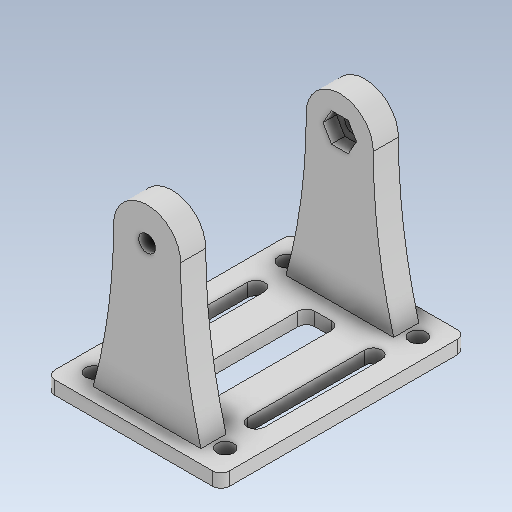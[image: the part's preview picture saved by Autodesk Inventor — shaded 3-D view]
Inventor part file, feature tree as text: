
AUTODESK INVENTOR PART (.ipt)
format: ipt  version: 2020 (Build 240168000, 168)  size: 212,992 bytes
history: native  units: in
note: dims shown in document units (in); Inventor stores cm internally (conversion verified against a paired STEP export)
features: sketch x11, other x3
ambient origin geometry x8: Origin, YZ Plane, XZ Plane, XY Plane, X Axis, Y Axis, Z Axis, Center Point
bodies: Solid1 (feature_tree)
feature tree (14):
  other  "sideArmsHolder.ipt"
  other  "Solid1::sideArmsHolder.ipt"
  other  "TaggingFeature1"
  sketch  "Sketch1"  dims[d0=0.3937in]
  sketch  "Sketch2"
  sketch  "Sketch3"
  sketch  "Sketch4"
  sketch  "Sketch6"
  sketch  "Sketch7"
  sketch  "Sketch10"
  sketch  "Sketch11"
  sketch  "Sketch12"
  sketch  "Sketch13"
  sketch  "Sketch14"
